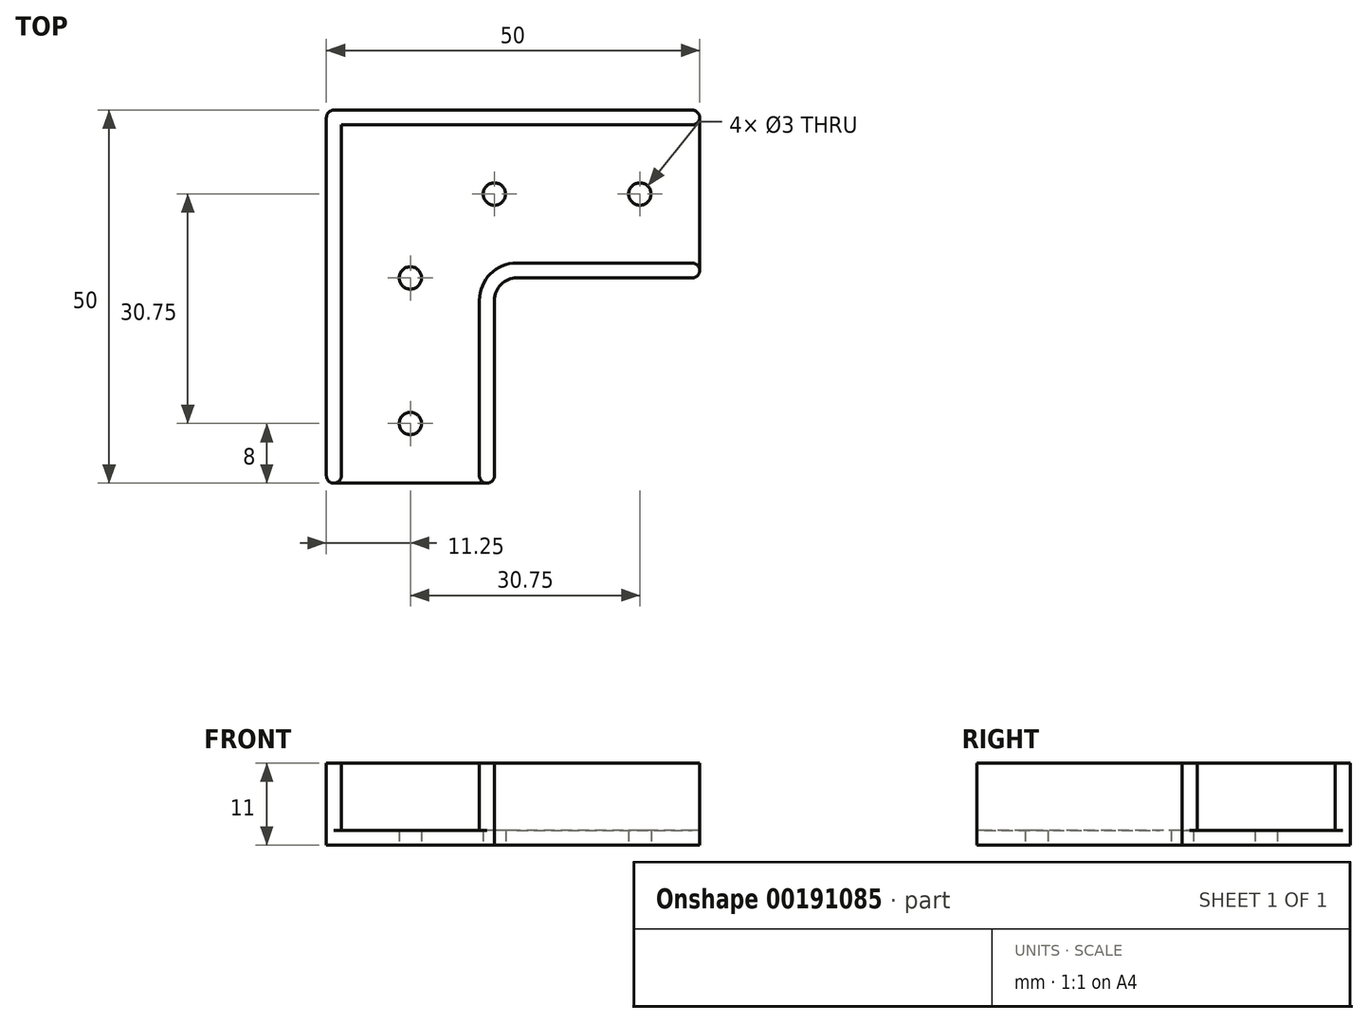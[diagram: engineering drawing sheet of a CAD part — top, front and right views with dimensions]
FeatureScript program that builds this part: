
annotation { "Feature Type Name" : "Feature", "Feature Type Description" : "" }
export const myFeature = defineFeature(function(context is Context, id is Id, definition is map)
    precondition{}
    {
        {
            var Q0;
            Q0=qCreatedBy(makeId("Top.planeOp"),FACE);
            var sketch = newSketch(context, id + "F0", { "sketchPlane" : qUnion([Q0])});
            skLineSegment(sketch, "E0.bottom", {"start": v(22.5, 0) * mm, "end": v(50, 0) * mm});
            skLineSegment(sketch, "E0.top", {"start": v(0, 22.5) * mm, "end": v(50, 22.5) * mm});
            skLineSegment(sketch, "E0.left", {"start": v(0, 0) * mm, "end": v(0, 22.5) * mm});
            skLineSegment(sketch, "E0.right", {"start": v(50, 0) * mm, "end": v(50, 22.5) * mm});
            skLineSegment(sketch, "E1.bottom", {"start": v(0, 22.5) * mm, "end": v(22.5, 22.5) * mm});
            skLineSegment(sketch, "E1.top", {"start": v(0, -27.5) * mm, "end": v(22.5, -27.5) * mm});
            skLineSegment(sketch, "E1.left", {"start": v(0, 22.5) * mm, "end": v(0, -27.5) * mm});
            skLineSegment(sketch, "E1.right", {"start": v(22.5, 0) * mm, "end": v(22.5, -27.5) * mm});
            skSolve(sketch);
        }
        {
            var Q0;
            Q0=makeQuery(id+"F0.imprint","IMPRINT",FACE,{"disambiguationData":[TD([[makeQuery(id+"F0.imprint","IMPRINT",EDGE,{"derivedFrom":sQuery(id+"F0.wireOp",EDGE,"E0.bottom")}),1.0]])]});
            extrude(context, id + "F1", {"entities" : qUnion([Q0]), "depth" : 2 * mm});
        }
        {
            var Q0;
            Q0=makeQuery(id+"F1.opExtrude","CAP_FACE",FACE,{"disambiguationData":[OSD([sQuery(id+"F0.wireOp",EDGE,"E0.bottom"),sQuery(id+"F0.wireOp",EDGE,"E0.top"),sQuery(id+"F0.wireOp",EDGE,"E0.right"),sQuery(id+"F0.wireOp",EDGE,"E1.bottom"),sQuery(id+"F0.wireOp",EDGE,"E1.top"),sQuery(id+"F0.wireOp",EDGE,"E1.left"),sQuery(id+"F0.wireOp",EDGE,"E1.right")])],"isStart":false});
            var sketch = newSketch(context, id + "F2", { "sketchPlane" : qUnion([Q0])});
            skLineSegment(sketch, "E2", {"start": v(50, 22.5) * mm, "end": v(0, 22.5) * mm});
            skLineSegment(sketch, "E3", {"start": v(0, 22.5) * mm, "end": v(0, -27.5) * mm});
            skLineSegment(sketch, "E4", {"start": v(22.5, -27.5) * mm, "end": v(22.5, 0) * mm});
            skLineSegment(sketch, "E5", {"start": v(22.5, 0) * mm, "end": v(50, 0) * mm});
            skLineSegment(sketch, "E6.0", {"start": v(2, 20.5) * mm, "end": v(2, -27.5) * mm});
            skLineSegment(sketch, "E6.1", {"start": v(50, 20.5) * mm, "end": v(2, 20.5) * mm});
            skLineSegment(sketch, "E7.0", {"start": v(20.5, 2) * mm, "end": v(50, 2) * mm});
            skLineSegment(sketch, "E7.1", {"start": v(20.5, -27.5) * mm, "end": v(20.5, 2) * mm});
            skLineSegment(sketch, "E8", {"start": v(50, 20.5) * mm, "end": v(50, 22.5) * mm});
            skLineSegment(sketch, "E9", {"start": v(50, 0) * mm, "end": v(50, 2) * mm});
            skLineSegment(sketch, "E10", {"start": v(22.5, -27.5) * mm, "end": v(20.5, -27.5) * mm});
            skLineSegment(sketch, "E11", {"start": v(2, -27.5) * mm, "end": v(0, -27.5) * mm});
            skSolve(sketch);
        }
        {
            var Q0;
            Q0 = qSketchRegion(id + "F2", true);
            extrude(context, id + "F3", {"entities" : qUnion([Q0]), "operationType" : NewBodyOperationType.ADD, "flatOperationType" : FlatOperationType.REMOVE, "offsetDistance" : 25 * mm, "depth" : 9 * mm, "domain" : OperationDomain.MODEL});
        }
        {
            var Q0;
            Q0=makeQuery(id+"F1.opExtrude","CAP_FACE",FACE,{"disambiguationData":[OSD([sQuery(id+"F0.wireOp",EDGE,"E0.bottom"),sQuery(id+"F0.wireOp",EDGE,"E0.top"),sQuery(id+"F0.wireOp",EDGE,"E0.right"),sQuery(id+"F0.wireOp",EDGE,"E1.bottom"),sQuery(id+"F0.wireOp",EDGE,"E1.top"),sQuery(id+"F0.wireOp",EDGE,"E1.left"),sQuery(id+"F0.wireOp",EDGE,"E1.right")])],"isStart":true});
            var sketch = newSketch(context, id + "F4", { "sketchPlane" : qUnion([Q0])});
            skLineSegment(sketch, "E12", {"start": v(11.25, 27.5) * mm, "end": v(11.25, -22.5) * mm, "construction": true});
            skLineSegment(sketch, "E13", {"start": v(50, -11.25) * mm, "end": v(0, -11.25) * mm, "construction": true});
            skCircle(sketch, "E14", {"center": v(11.25, 19.5) * mm, "radius": 1.5 * mm});
            skCircle(sketch, "E15", {"center": v(11.25, 0) * mm, "radius": 1.5 * mm});
            skCircle(sketch, "E16", {"center": v(22.5, -11.25) * mm, "radius": 1.5 * mm});
            skCircle(sketch, "E17", {"center": v(42, -11.25) * mm, "radius": 1.5 * mm});
            skSolve(sketch);
        }
        {
            var Q0;
            Q0 = qSketchRegion(id + "F4", true);
            extrude(context, id + "F5", {"entities" : qUnion([Q0]), "operationType" : NewBodyOperationType.REMOVE, "endBound" : BoundingType.UP_TO_NEXT, "oppositeDirection" : true, "depth" : 25 * mm});
        }
        {
            var Q0;
            Q0=makeQuery(id+"F3.boolean.opBoolean","MERGE",EDGE,{"derivedFrom":[makeQuery(id+"F1.opExtrude","SWEPT_EDGE",EDGE,{"disambiguationData":[OSD([sQuery(id+"F0.wireOp",EDGE,"E0.bottom"),sQuery(id+"F0.wireOp",EDGE,"E1.right")])]}),makeQuery(id+"F3.opExtrude","SWEPT_EDGE",EDGE,{"disambiguationData":[OSD([sQuery(id+"F2.wireOp",EDGE,"E4"),sQuery(id+"F2.wireOp",EDGE,"E5")])]})]});
            fillet(context, id + "F6", {"entities" : qUnion([Q0]), "radius" : 3 * mm, "tangentPropagation" : true, "allowEdgeOverflow" : false});
        }
        {
            var Q0;
            Q0=makeQuery(id+"F3.opExtrude","SWEPT_EDGE",EDGE,{"disambiguationData":[OSD([sQuery(id+"F0.wireOp",EDGE,"E1.top"),sQuery(id+"F2.wireOp",EDGE,"E6.0"),sQuery(id+"F2.wireOp",EDGE,"E11")])]});
            var Q1;
            Q1=makeQuery(id+"F3.boolean.opBoolean","MERGE",EDGE,{"derivedFrom":[makeQuery(id+"F1.opExtrude","SWEPT_EDGE",EDGE,{"disambiguationData":[OSD([sQuery(id+"F0.wireOp",EDGE,"E1.top"),sQuery(id+"F0.wireOp",EDGE,"E1.right")])]}),makeQuery(id+"F3.opExtrude","SWEPT_EDGE",EDGE,{"disambiguationData":[OSD([sQuery(id+"F2.wireOp",EDGE,"E4"),sQuery(id+"F2.wireOp",EDGE,"E10")])]})]});
            var Q2;
            Q2=makeQuery(id+"F3.opExtrude","SWEPT_EDGE",EDGE,{"disambiguationData":[OSD([sQuery(id+"F0.wireOp",EDGE,"E1.top"),sQuery(id+"F2.wireOp",EDGE,"E7.1"),sQuery(id+"F2.wireOp",EDGE,"E10")])]});
            var Q3;
            Q3=makeQuery(id+"F3.boolean.opBoolean","MERGE",EDGE,{"derivedFrom":[makeQuery(id+"F1.opExtrude","SWEPT_EDGE",EDGE,{"disambiguationData":[OSD([sQuery(id+"F0.wireOp",EDGE,"E1.top"),sQuery(id+"F0.wireOp",EDGE,"E1.left")])]}),makeQuery(id+"F3.opExtrude","SWEPT_EDGE",EDGE,{"disambiguationData":[OSD([sQuery(id+"F2.wireOp",EDGE,"E3"),sQuery(id+"F2.wireOp",EDGE,"E11")])]})]});
            var Q4;
            Q4=makeQuery(id+"F3.boolean.opBoolean","MERGE",EDGE,{"derivedFrom":[makeQuery(id+"F1.opExtrude","SWEPT_EDGE",EDGE,{"disambiguationData":[OSD([sQuery(id+"F0.wireOp",EDGE,"E1.bottom"),sQuery(id+"F0.wireOp",EDGE,"E1.left")])]}),makeQuery(id+"F3.opExtrude","SWEPT_EDGE",EDGE,{"disambiguationData":[OSD([sQuery(id+"F2.wireOp",EDGE,"E2"),sQuery(id+"F2.wireOp",EDGE,"E3")])]})]});
            var Q5;
            Q5=makeQuery(id+"F3.boolean.opBoolean","MERGE",EDGE,{"derivedFrom":[makeQuery(id+"F1.opExtrude","SWEPT_EDGE",EDGE,{"disambiguationData":[OSD([sQuery(id+"F0.wireOp",EDGE,"E0.top"),sQuery(id+"F0.wireOp",EDGE,"E0.right")])]}),makeQuery(id+"F3.opExtrude","SWEPT_EDGE",EDGE,{"disambiguationData":[OSD([sQuery(id+"F2.wireOp",EDGE,"E2"),sQuery(id+"F2.wireOp",EDGE,"E8")])]})]});
            var Q6;
            Q6=makeQuery(id+"F3.opExtrude","SWEPT_EDGE",EDGE,{"disambiguationData":[OSD([sQuery(id+"F0.wireOp",EDGE,"E0.right"),sQuery(id+"F2.wireOp",EDGE,"E6.1"),sQuery(id+"F2.wireOp",EDGE,"E8")])]});
            var Q7;
            Q7=makeQuery(id+"F3.boolean.opBoolean","MERGE",EDGE,{"derivedFrom":[makeQuery(id+"F1.opExtrude","SWEPT_EDGE",EDGE,{"disambiguationData":[OSD([sQuery(id+"F0.wireOp",EDGE,"E0.bottom"),sQuery(id+"F0.wireOp",EDGE,"E0.right")])]}),makeQuery(id+"F3.opExtrude","SWEPT_EDGE",EDGE,{"disambiguationData":[OSD([sQuery(id+"F2.wireOp",EDGE,"E5"),sQuery(id+"F2.wireOp",EDGE,"E9")])]})]});
            var Q8;
            Q8=makeQuery(id+"F3.opExtrude","SWEPT_EDGE",EDGE,{"disambiguationData":[OSD([sQuery(id+"F0.wireOp",EDGE,"E0.right"),sQuery(id+"F2.wireOp",EDGE,"E7.0"),sQuery(id+"F2.wireOp",EDGE,"E9")])]});
            fillet(context, id + "F7", {"entities" : qUnion([Q0, Q1, Q2, Q3, Q4, Q5, Q6, Q7, Q8]), "radius" : 1 * mm, "tangentPropagation" : true, "allowEdgeOverflow" : false});
        }
        {
            var Q0;
            Q0=makeQuery(id+"F3.opExtrude","SWEPT_EDGE",EDGE,{"disambiguationData":[OSD([sQuery(id+"F2.wireOp",EDGE,"E7.0"),sQuery(id+"F2.wireOp",EDGE,"E7.1")])]});
            fillet(context, id + "F8", {"entities" : qUnion([Q0]), "radius" : 5 * mm, "tangentPropagation" : true, "allowEdgeOverflow" : false});
        }
    });
